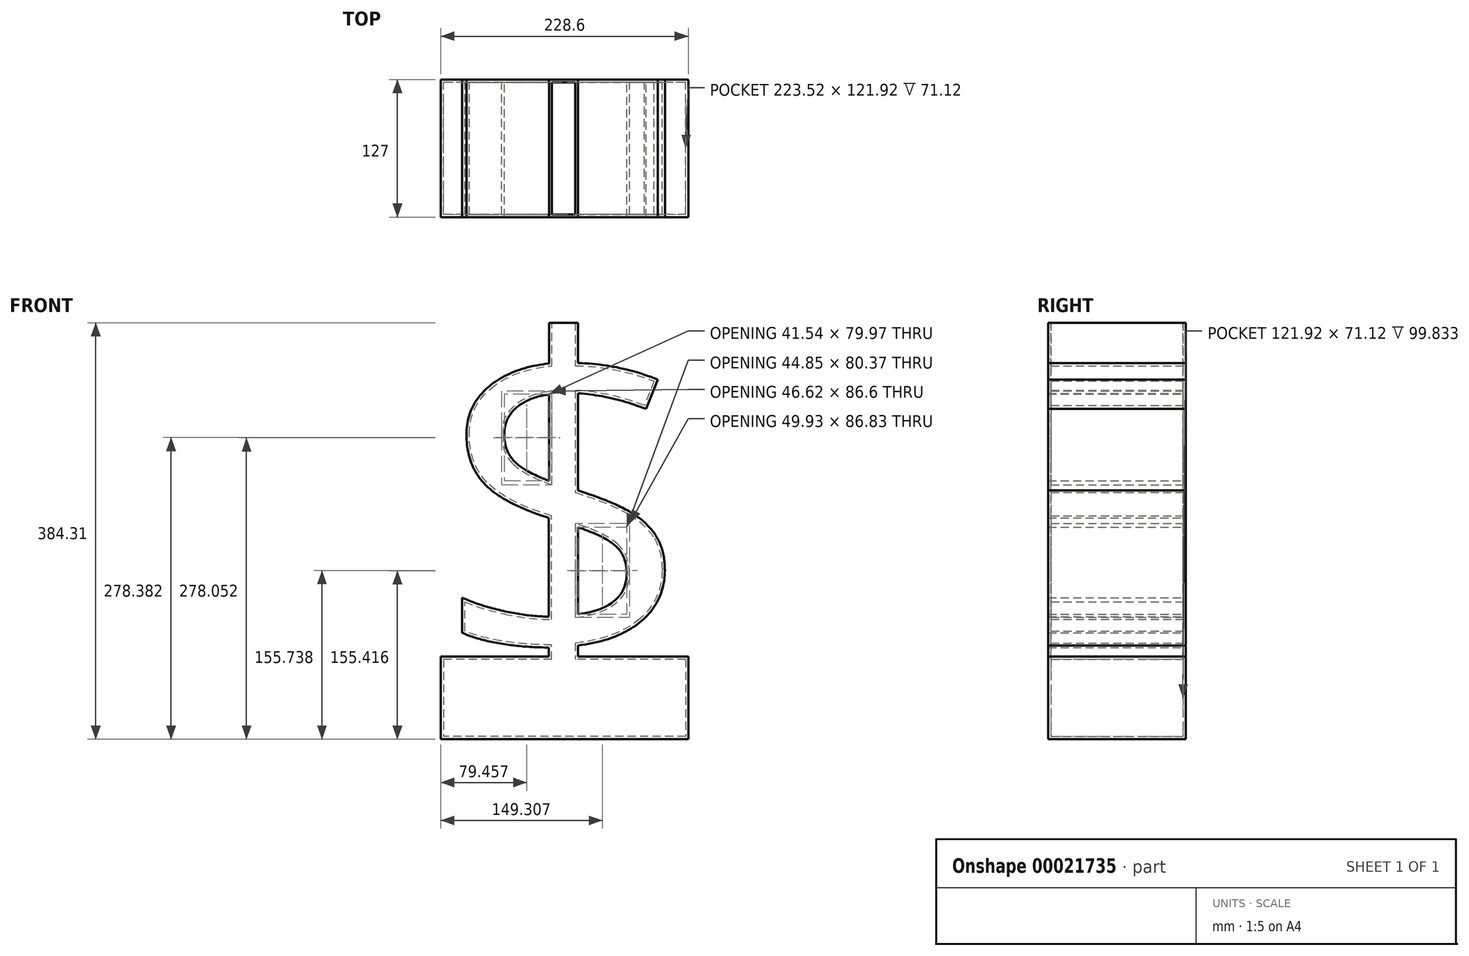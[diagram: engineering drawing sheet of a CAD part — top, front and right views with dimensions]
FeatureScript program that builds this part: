
annotation { "Feature Type Name" : "Feature", "Feature Type Description" : "" }
export const myFeature = defineFeature(function(context is Context, id is Id, definition is map)
    precondition{}
    {
        {
            var Q0;
            Q0=qCreatedBy(makeId("Front.planeOp"),FACE);
            var sketch = newSketch(context, id + "F0", { "sketchPlane" : qUnion([Q0])});
            skText(sketch, "E0", { "text": "$", "fontName": "OpenSans-Regular.ttf"});
            skLineSegment(sketch, "E1.rect.bottom", {"start": v(114.3, -139.08) * mm, "end": v(-114.3, -139.08) * mm});
            skLineSegment(sketch, "E1.rect.top", {"start": v(114.3, -215.28) * mm, "end": v(-114.3, -215.28) * mm});
            skLineSegment(sketch, "E1.rect.left", {"start": v(114.3, -139.08) * mm, "end": v(114.3, -215.28) * mm});
            skLineSegment(sketch, "E1.rect.right", {"start": v(-114.3, -139.08) * mm, "end": v(-114.3, -215.28) * mm});
            skPoint(sketch, "E1.rect.middle", {"position": v(0, -177.18) * mm});
            skLineSegment(sketch, "E2", {"start": v(-14.47, -139.08) * mm, "end": v(-14.47, 165.72) * mm});
            const initialGuessF0  = {"E0": [-0.12156, -0.15217, 1, 0, 0.3048]};
            skSetInitialGuess(sketch, initialGuessF0);
            skSolve(sketch);
        }
        {
            var Q0;
            Q0 = qSketchRegion(id + "F0", true);
            var Q1;
            Q1 = qSketchRegion(id + "F0", true);
            extrude(context, id + "F1", {"entities" : qUnion([Q0, Q1]), "depth" : 127 * mm});
        }
        {
            var Q0;
            Q0=makeQuery(id+"F1.opExtrude","SWEPT_FACE",FACE,{"disambiguationData":[OSD([sQuery(id+"F0.wireOp",EDGE,"E0.sketch_text.stroke-16")])]});
            shell(context, id + "F2", {"entities" : qUnion([Q0]), "thickness" : 2.54 * mm});
        }
    });
